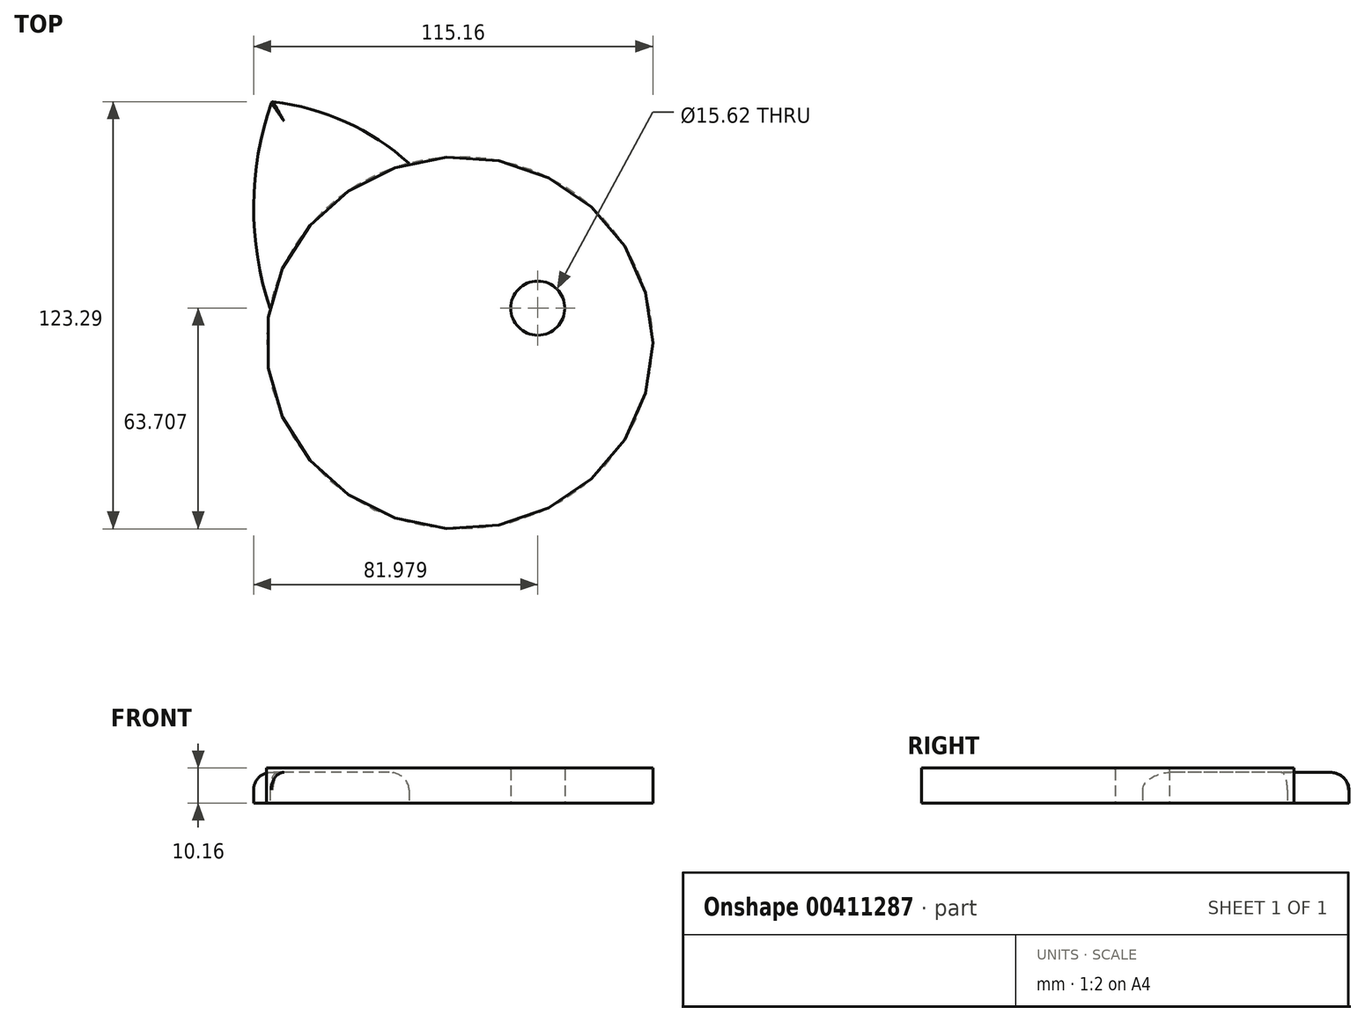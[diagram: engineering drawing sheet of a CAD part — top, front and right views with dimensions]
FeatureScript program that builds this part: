
annotation { "Feature Type Name" : "Feature", "Feature Type Description" : "" }
export const myFeature = defineFeature(function(context is Context, id is Id, definition is map)
    precondition{}
    {
        {
            var Q0;
            Q0=qCreatedBy(makeId("Top.planeOp"),FACE);
            var sketch = newSketch(context, id + "F0", { "sketchPlane" : qUnion([Q0])});
            skEllipse(sketch, "E0", {"center": v(0, 0) * mm, "majorRadius": 55.71 * mm, "minorRadius": 53.7 * mm, "majorAxis": v(1, 0)});
            skArc(sketch, "E1", {"start": v(-54.2, 69.64) * mm, "mid": v(-59.45, 39.87) * mm, "end": v(-54.73, 10.02) * mm});
            skArc(sketch, "E2", {"start": v(-14.6, 51.81) * mm, "mid": v(-33.02, 63.82) * mm, "end": v(-54.2, 69.64) * mm});
            skArc(sketch, "E3.MirrorCS", {"start": v(14.6, 51.81) * mm, "mid": v(33.02, 63.82) * mm, "end": v(54.2, 69.64) * mm});
            skArc(sketch, "E4.MirrorCS", {"start": v(54.2, 69.64) * mm, "mid": v(59.45, 39.87) * mm, "end": v(54.73, 10.02) * mm});
            skCircle(sketch, "E5", {"center": v(-22.53, 10.02) * mm, "radius": 7.8 * mm});
            skCircle(sketch, "E6.MirrorC", {"center": v(22.53, 10.02) * mm, "radius": 7.8 * mm});
            skLineSegment(sketch, "E7", {"start": v(0, -11.68) * mm, "end": v(-5.05, -11.68) * mm});
            skLineSegment(sketch, "E8", {"start": v(-5.05, -11.68) * mm, "end": v(0, -15.01) * mm});
            skLineSegment(sketch, "E9.MirrorCS", {"start": v(0, -11.68) * mm, "end": v(5.05, -11.68) * mm});
            skLineSegment(sketch, "E10.MirrorCS", {"start": v(5.05, -11.68) * mm, "end": v(0, -15.01) * mm});
            skArc(sketch, "E11", {"start": v(-12.32, -20.46) * mm, "mid": v(-6.22, -23.2) * mm, "end": v(0, -20.77) * mm});
            skArc(sketch, "E12.0", {"start": v(-13.43, -21.5) * mm, "mid": v(-6.26, -24.72) * mm, "end": v(1.06, -21.86) * mm});
            skArc(sketch, "E13", {"start": v(-12.32, -20.46) * mm, "mid": v(-13.35, -20.48) * mm, "end": v(-13.43, -21.5) * mm});
            skArc(sketch, "E14.MirrorCS", {"start": v(12.32, -20.46) * mm, "mid": v(6.22, -23.2) * mm, "end": v(0, -20.77) * mm});
            skArc(sketch, "E15.MirrorCS", {"start": v(13.43, -21.5) * mm, "mid": v(6.26, -24.72) * mm, "end": v(-1.06, -21.86) * mm});
            skArc(sketch, "E16.MirrorCS", {"start": v(12.32, -20.46) * mm, "mid": v(13.35, -20.48) * mm, "end": v(13.43, -21.5) * mm});
            skArc(sketch, "E17", {"start": v(-1.79, -22.1) * mm, "mid": v(-0.9, -20.39) * mm, "end": v(-0.58, -18.48) * mm});
            skArc(sketch, "E18", {"start": v(0, -17.77) * mm, "mid": v(-0.45, -18) * mm, "end": v(-0.58, -18.48) * mm});
            skArc(sketch, "E19.MirrorCS", {"start": v(1.79, -22.1) * mm, "mid": v(0.9, -20.39) * mm, "end": v(0.58, -18.48) * mm});
            skArc(sketch, "E20.MirrorCS", {"start": v(0, -17.77) * mm, "mid": v(0.45, -18) * mm, "end": v(0.58, -18.48) * mm});
            skLineSegment(sketch, "E21", {"start": v(0, -6.47) * mm, "end": v(0, 9.21) * mm});
            skLineSegment(sketch, "E22", {"start": v(7.52, 0) * mm, "end": v(-10.78, 0) * mm});
            skSolve(sketch);
        }
        {
            var Q0;
            Q0=makeQuery(id+"F0.imprint","IMPRINT",FACE,{"disambiguationData":[TD([[makeQuery(id+"F0.imprint","IMPRINT",EDGE,{"derivedFrom":sQuery(id+"F0.wireOp",EDGE,"E5")}),-1.0]])]});
            var Q1;
            {var subQ0=sQuery(id+"F0.wireOp",EDGE,"E1");Q1=makeQuery(id+"F0.imprint","IMPRINT",FACE,{"disambiguationData":[TD([[makeQuery(id+"F0.imprint","IMPRINT",EDGE,{"derivedFrom":subQ0}),1.0]])]});}
            var Q2;
            {var subQ0=sQuery(id+"F0.wireOp",EDGE,"E3.MirrorCS");Q2=makeQuery(id+"F0.imprint","IMPRINT",FACE,{"disambiguationData":[TD([[makeQuery(id+"F0.imprint","IMPRINT",EDGE,{"derivedFrom":subQ0}),-1.0]])]});}
            extrude(context, id + "F1", {"entities" : qUnion([Q0, Q1, Q2]), "depth" : 8.9 * mm});
        }
        {
            var Q0;
            Q0=makeQuery(id+"F0.imprint","IMPRINT",FACE,{"disambiguationData":[TD([[makeQuery(id+"F0.imprint","IMPRINT",EDGE,{"derivedFrom":sQuery(id+"F0.wireOp",EDGE,"E5")}),1.0]])]});
            var Q1;
            Q1=makeQuery(id+"F0.imprint","IMPRINT",FACE,{"disambiguationData":[TD([[makeQuery(id+"F0.imprint","IMPRINT",EDGE,{"derivedFrom":sQuery(id+"F0.wireOp",EDGE,"E6.MirrorC")}),-1.0]])]});
            var Q2;
            Q2=makeQuery(id+"F0.imprint","IMPRINT",FACE,{"disambiguationData":[TD([[makeQuery(id+"F0.imprint","IMPRINT",EDGE,{"derivedFrom":sQuery(id+"F0.wireOp",EDGE,"E7")}),1.0]])]});
            var Q3;
            {var subQ0=sQuery(id+"F0.wireOp",EDGE,"E13");Q3=makeQuery(id+"F0.imprint","IMPRINT",FACE,{"disambiguationData":[TD([[makeQuery(id+"F0.imprint","IMPRINT",EDGE,{"derivedFrom":subQ0}),1.0]])]});}
            var Q4;
            {var subQ0=sQuery(id+"F0.wireOp",EDGE,"E17");Q4=makeQuery(id+"F0.imprint","IMPRINT",FACE,{"disambiguationData":[TD([[makeQuery(id+"F0.imprint","IMPRINT",EDGE,{"derivedFrom":subQ0}),-1.0]])]});}
            extrude(context, id + "F2", {"entities" : qUnion([Q0, Q1, Q2, Q3, Q4]), "operationType" : NewBodyOperationType.ADD, "depth" : 10.16 * mm});
        }
        {
            var Q0;
            Q0=makeQuery(id+"F2.opExtrude","CAP_EDGE",EDGE,{"disambiguationData":[OSD([sQuery(id+"F0.wireOp",EDGE,"E5")])],"isStart":false});
            var Q1;
            Q1=makeQuery(id+"F2.opExtrude","CAP_EDGE",EDGE,{"disambiguationData":[OSD([sQuery(id+"F0.wireOp",EDGE,"E8")])],"isStart":false});
            var Q2;
            Q2=makeQuery(id+"F2.opExtrude","CAP_EDGE",EDGE,{"disambiguationData":[OSD([sQuery(id+"F0.wireOp",EDGE,"E7"),sQuery(id+"F0.wireOp",EDGE,"E9.MirrorCS")])],"isStart":false});
            var Q3;
            Q3=makeQuery(id+"F2.opExtrude","CAP_EDGE",EDGE,{"disambiguationData":[OSD([sQuery(id+"F0.wireOp",EDGE,"E10.MirrorCS")])],"isStart":false});
            var Q4;
            Q4=makeQuery(id+"F2.opExtrude","CAP_EDGE",EDGE,{"disambiguationData":[OSD([sQuery(id+"F0.wireOp",EDGE,"E6.MirrorC")])],"isStart":false});
            var Q5;
            Q5=makeQuery(id+"F2.opExtrude","CAP_EDGE",EDGE,{"disambiguationData":[OSD([sQuery(id+"F0.wireOp",EDGE,"E12.0")])],"isStart":false});
            var Q6;
            Q6=makeQuery(id+"F2.opExtrude","CAP_EDGE",EDGE,{"disambiguationData":[OSD([sQuery(id+"F0.wireOp",EDGE,"E15.MirrorCS")])],"isStart":false});
            var Q7;
            Q7=makeQuery(id+"F2.opExtrude","CAP_EDGE",EDGE,{"disambiguationData":[OSD([sQuery(id+"F0.wireOp",EDGE,"E19.MirrorCS")])],"isStart":false});
            var Q8;
            Q8=makeQuery(id+"F2.opExtrude","CAP_EDGE",EDGE,{"disambiguationData":[OSD([sQuery(id+"F0.wireOp",EDGE,"E14.MirrorCS")])],"isStart":false});
            var Q9;
            Q9=makeQuery(id+"F2.opExtrude","CAP_EDGE",EDGE,{"disambiguationData":[OSD([sQuery(id+"F0.wireOp",EDGE,"E17")])],"isStart":false});
            var Q10;
            Q10=makeQuery(id+"F2.opExtrude","CAP_EDGE",EDGE,{"disambiguationData":[OSD([sQuery(id+"F0.wireOp",EDGE,"E11")])],"isStart":false});
            var Q11;
            Q11=makeQuery(id+"F2.opExtrude","CAP_EDGE",EDGE,{"disambiguationData":[OSD([sQuery(id+"F0.wireOp",EDGE,"E18")])],"isStart":false});
            var Q12;
            Q12=makeQuery(id+"F2.opExtrude","CAP_EDGE",EDGE,{"disambiguationData":[OSD([sQuery(id+"F0.wireOp",EDGE,"E20.MirrorCS")])],"isStart":false});
            var Q13;
            Q13=makeQuery(id+"F2.opExtrude","CAP_EDGE",EDGE,{"disambiguationData":[OSD([sQuery(id+"F0.wireOp",EDGE,"E13")])],"isStart":false});
            var Q14;
            Q14=makeQuery(id+"F2.opExtrude","CAP_EDGE",EDGE,{"disambiguationData":[OSD([sQuery(id+"F0.wireOp",EDGE,"E16.MirrorCS")])],"isStart":false});
            fillet(context, id + "F3", {"entities" : qUnion([Q0, Q1, Q2, Q3, Q4, Q5, Q6, Q7, Q8, Q9, Q10, Q11, Q12, Q13, Q14]), "radius" : 0.5 * mm, "tangentPropagation" : true, "allowEdgeOverflow" : false});
        }
        {
            var Q0;
            {var subQ0=sQuery(id+"F0.wireOp",EDGE,"E0");Q0=makeQuery(id+"F1.opExtrude","CAP_EDGE",EDGE,{"disambiguationData":[OSD([subQ0]),TDD([makeQuery(id+"F0.imprint","IMPRINT",EDGE,{"disambiguationData":[TD([[makeQuery(id+"F0.imprint","INTERSECT",VERTEX,{"derivedFrom":[subQ0,sQuery(id+"F0.wireOp",EDGE,"E2")]}),1.0]])],"derivedFrom":subQ0})])],"isStart":false});}
            var Q1;
            Q1=makeQuery(id+"F1.opExtrude","CAP_EDGE",EDGE,{"disambiguationData":[OSD([sQuery(id+"F0.wireOp",EDGE,"E2")])],"isStart":false});
            var Q2;
            Q2=makeQuery(id+"F1.opExtrude","CAP_EDGE",EDGE,{"disambiguationData":[OSD([sQuery(id+"F0.wireOp",EDGE,"E3.MirrorCS")])],"isStart":false});
            var Q3;
            Q3=makeQuery(id+"F1.opExtrude","CAP_EDGE",EDGE,{"disambiguationData":[OSD([sQuery(id+"F0.wireOp",EDGE,"E1")])],"isStart":false});
            var Q4;
            {var subQ0=sQuery(id+"F0.wireOp",EDGE,"E0");Q4=makeQuery(id+"F1.opExtrude","CAP_EDGE",EDGE,{"disambiguationData":[OSD([subQ0]),TDD([makeQuery(id+"F0.imprint","IMPRINT",EDGE,{"disambiguationData":[TD([[makeQuery(id+"F0.imprint","INTERSECT",VERTEX,{"derivedFrom":[subQ0,sQuery(id+"F0.wireOp",EDGE,"E1")]}),-1.0]])],"derivedFrom":subQ0})])],"isStart":false});}
            var Q5;
            Q5=makeQuery(id+"F1.opExtrude","CAP_EDGE",EDGE,{"disambiguationData":[OSD([sQuery(id+"F0.wireOp",EDGE,"E4.MirrorCS")])],"isStart":false});
            fillet(context, id + "F4", {"entities" : qUnion([Q0, Q1, Q2, Q3, Q4, Q5]), "radius" : 5.08 * mm, "tangentPropagation" : true, "allowEdgeOverflow" : false});
        }
        {
            var Q0;
            Q0=makeQuery(id+"F4.opFillet","BLEND_EDGE",EDGE,{"blendedFrom":[makeQuery(id+"F1.opExtrude","CAP_EDGE",EDGE,{"disambiguationData":[OSD([sQuery(id+"F0.wireOp",EDGE,"E1")])],"isStart":false}),makeQuery(id+"F1.opExtrude","CAP_EDGE",EDGE,{"disambiguationData":[OSD([sQuery(id+"F0.wireOp",EDGE,"E2")])],"isStart":false})],"blendedInto":[]});
            var Q1;
            Q1=makeQuery(id+"F4.opFillet","BLEND_EDGE",EDGE,{"blendedFrom":[makeQuery(id+"F1.opExtrude","CAP_EDGE",EDGE,{"disambiguationData":[OSD([sQuery(id+"F0.wireOp",EDGE,"E3.MirrorCS")])],"isStart":false}),makeQuery(id+"F1.opExtrude","CAP_EDGE",EDGE,{"disambiguationData":[OSD([sQuery(id+"F0.wireOp",EDGE,"E4.MirrorCS")])],"isStart":false})],"blendedInto":[]});
            fillet(context, id + "F5", {"entities" : qUnion([Q0, Q1]), "radius" : 0.5 * mm, "tangentPropagation" : true, "allowEdgeOverflow" : false});
        }
    });
